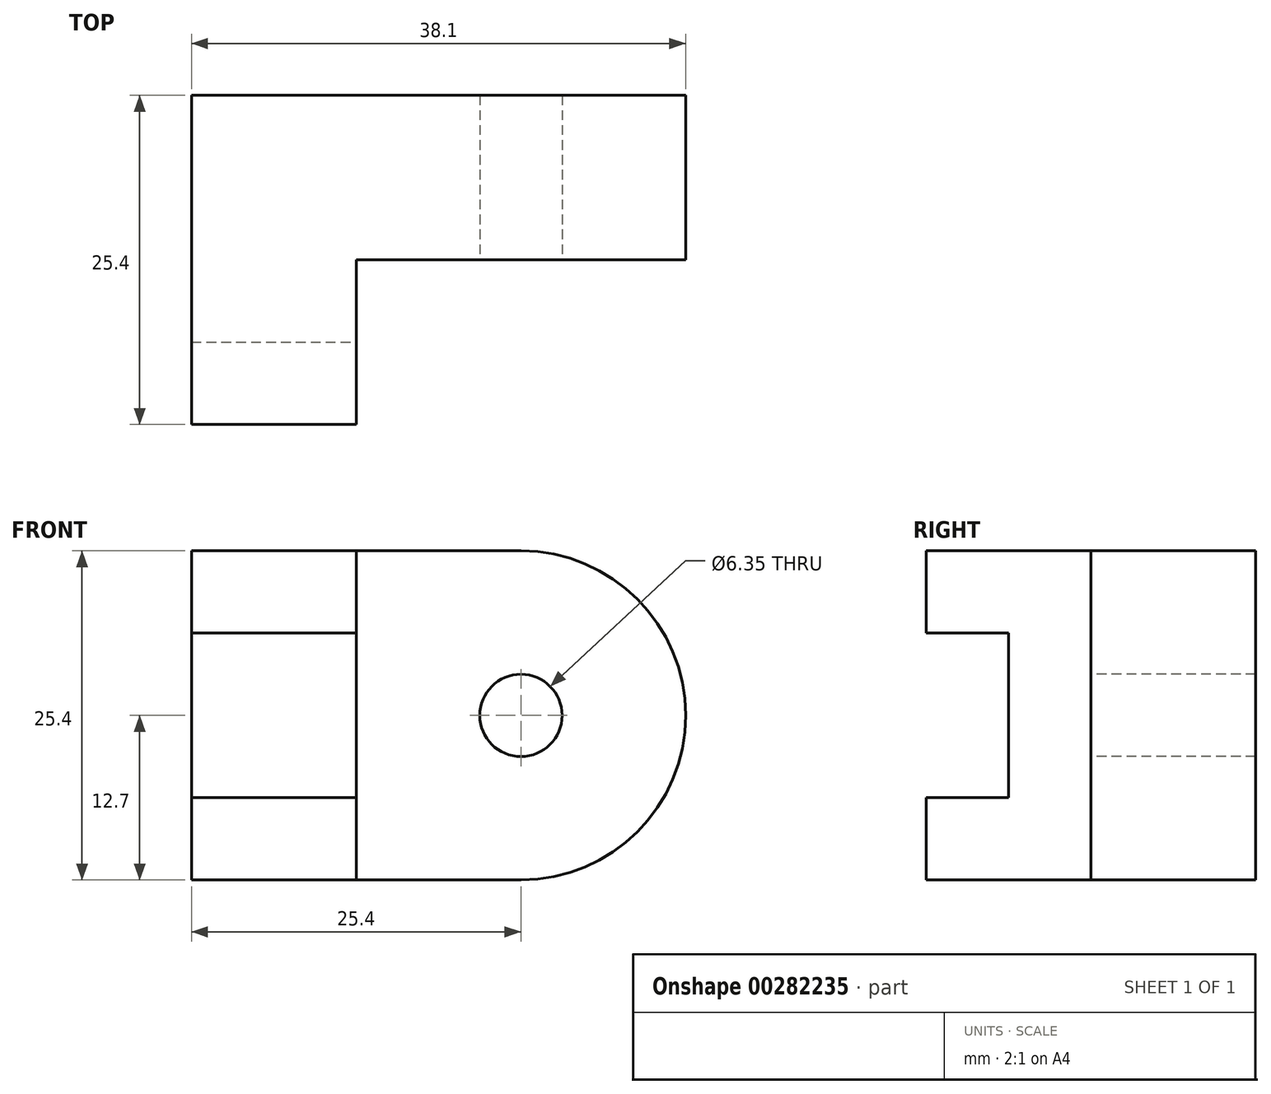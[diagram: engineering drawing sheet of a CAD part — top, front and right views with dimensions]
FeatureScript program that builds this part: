
annotation { "Feature Type Name" : "Feature", "Feature Type Description" : "" }
export const myFeature = defineFeature(function(context is Context, id is Id, definition is map)
    precondition{}
    {
        {
            var Q0;
            Q0=qCreatedBy(makeId("Front.planeOp"),FACE);
            var sketch = newSketch(context, id + "F0", { "sketchPlane" : qUnion([Q0])});
            skLineSegment(sketch, "E0.bottom", {"start": v(0, 0) * mm, "end": v(-12.7, 0) * mm});
            skLineSegment(sketch, "E0.top", {"start": v(0, 25.4) * mm, "end": v(-12.7, 25.4) * mm});
            skLineSegment(sketch, "E0.left", {"start": v(0, 0) * mm, "end": v(0, 25.4) * mm});
            skLineSegment(sketch, "E0.right", {"start": v(-12.7, 0) * mm, "end": v(-12.7, 25.4) * mm});
            skSolve(sketch);
        }
        {
            var Q0;
            Q0 = qSketchRegion(id + "F0", true);
            extrude(context, id + "F1", {"entities" : qUnion([Q0]), "endBound" : BoundingType.SYMMETRIC, "oppositeDirection" : true, "depth" : 25.4 * mm});
        }
        {
            var Q0;
            Q0=qCreatedBy(makeId("Right.planeOp"),FACE);
            var sketch = newSketch(context, id + "F2", { "sketchPlane" : qUnion([Q0])});
            skLineSegment(sketch, "E1.bottom", {"start": v(-12.7, 19.05) * mm, "end": v(-6.35, 19.05) * mm});
            skLineSegment(sketch, "E1.top", {"start": v(-12.7, 6.35) * mm, "end": v(-6.35, 6.35) * mm});
            skLineSegment(sketch, "E1.left", {"start": v(-12.7, 19.05) * mm, "end": v(-12.7, 6.35) * mm});
            skLineSegment(sketch, "E1.right", {"start": v(-6.35, 19.05) * mm, "end": v(-6.35, 6.35) * mm});
            skSolve(sketch);
        }
        {
            var Q0;
            Q0 = qSketchRegion(id + "F2", true);
            extrude(context, id + "F3", {"entities" : qUnion([Q0]), "operationType" : NewBodyOperationType.REMOVE, "oppositeDirection" : true, "depth" : 12.7 * mm});
        }
        {
            var Q0;
            Q0=makeQuery(id+"F1.opExtrude","SWEPT_FACE",FACE,{"disambiguationData":[OSD([sQuery(id+"F0.wireOp",EDGE,"E0.left")])]});
            var sketch = newSketch(context, id + "F4", { "sketchPlane" : qUnion([Q0])});
            skLineSegment(sketch, "E2.bottom", {"start": v(12.7, 25.4) * mm, "end": v(0, 25.4) * mm});
            skLineSegment(sketch, "E2.top", {"start": v(12.7, 0) * mm, "end": v(0, 0) * mm});
            skLineSegment(sketch, "E2.left", {"start": v(12.7, 25.4) * mm, "end": v(12.7, 0) * mm});
            skLineSegment(sketch, "E2.right", {"start": v(0, 25.4) * mm, "end": v(0, 0) * mm});
            skSolve(sketch);
        }
        {
            var Q0;
            Q0 = qSketchRegion(id + "F4", true);
            extrude(context, id + "F5", {"entities" : qUnion([Q0]), "operationType" : NewBodyOperationType.ADD, "depth" : 12.7 * mm});
        }
        {
            var Q0;
            Q0=makeQuery(id+"F5.opExtrude","SWEPT_FACE",FACE,{"disambiguationData":[OSD([sQuery(id+"F4.wireOp",EDGE,"E2.right")])]});
            var sketch = newSketch(context, id + "F6", { "sketchPlane" : qUnion([Q0])});
            skArc(sketch, "E3", {"start": v(12.7, 0) * mm, "mid": v(25.4, 12.7) * mm, "end": v(12.7, 25.4) * mm});
            skSolve(sketch);
        }
        {
            var Q0;
            Q0 = qSketchRegion(id + "F6", true);
            var Q1;
            Q1=makeQuery(id+"F6.imprint","IMPRINT",FACE,{"disambiguationData":[TD([[makeQuery(id+"F6.imprint","IMPRINT",EDGE,{"derivedFrom":sQuery(id+"F6.wireOp",EDGE,"E3")}),1.0]])]});
            extrude(context, id + "F7", {"entities" : qUnion([Q0, Q1]), "operationType" : NewBodyOperationType.ADD, "oppositeDirection" : true, "depth" : 12.7 * mm});
        }
        {
            var Q0;
            {var subQ0=sQuery(id+"F4.wireOp",EDGE,"E2.right");Q0=makeQuery(id+"F7.boolean.opBoolean","MERGE",FACE,{"derivedFrom":[makeQuery(id+"F5.opExtrude","SWEPT_FACE",FACE,{"disambiguationData":[OSD([subQ0])]}),makeQuery(id+"F7.opExtrude","CAP_FACE",FACE,{"disambiguationData":[OSD([subQ0,sQuery(id+"F6.wireOp",EDGE,"E3")])],"isStart":true})]});}
            var sketch = newSketch(context, id + "F8", { "sketchPlane" : qUnion([Q0])});
            skCircle(sketch, "E4", {"center": v(12.7, 12.7) * mm, "radius": 3.18 * mm});
            skSolve(sketch);
        }
        {
            var Q0;
            Q0=makeQuery(id+"F8.imprint","IMPRINT",FACE,{"disambiguationData":[TD([[makeQuery(id+"F8.imprint","IMPRINT",EDGE,{"derivedFrom":sQuery(id+"F8.wireOp",EDGE,"E4")}),1.0]])]});
            extrude(context, id + "F9", {"entities" : qUnion([Q0]), "operationType" : NewBodyOperationType.REMOVE, "oppositeDirection" : true, "depth" : 12.7 * mm});
        }
    });
